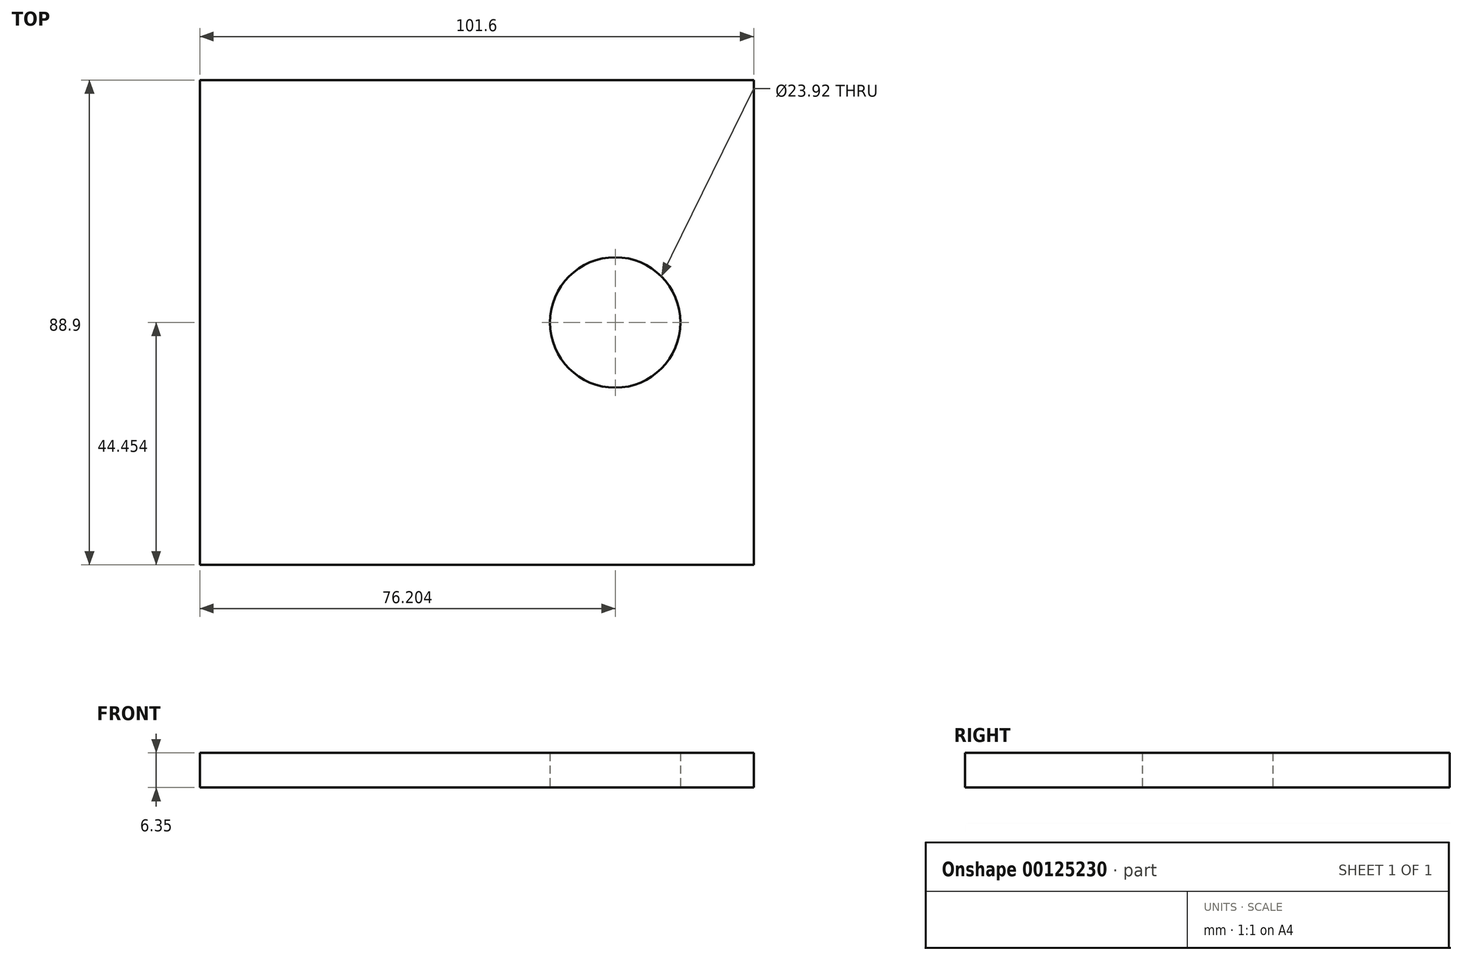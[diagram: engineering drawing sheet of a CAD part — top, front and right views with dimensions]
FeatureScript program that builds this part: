
annotation { "Feature Type Name" : "Feature", "Feature Type Description" : "" }
export const myFeature = defineFeature(function(context is Context, id is Id, definition is map)
    precondition{}
    {
        {
            var Q0;
            Q0=qCreatedBy(makeId("Top.planeOp"),FACE);
            var sketch = newSketch(context, id + "F0", { "sketchPlane" : qUnion([Q0])});
            skLineSegment(sketch, "E0.bottom", {"start": v(-45.86, 38.73) * mm, "end": v(55.74, 38.73) * mm});
            skLineSegment(sketch, "E0.top", {"start": v(-45.86, -50.17) * mm, "end": v(55.74, -50.17) * mm});
            skLineSegment(sketch, "E0.left", {"start": v(-45.86, 38.73) * mm, "end": v(-45.86, -50.17) * mm});
            skLineSegment(sketch, "E0.right", {"start": v(55.74, 38.73) * mm, "end": v(55.74, -50.17) * mm});
            skLineSegment(sketch, "E1", {"start": v(4.94, 38.73) * mm, "end": v(55.74, 38.73) * mm});
            skCircle(sketch, "E2", {"center": v(30.34, -5.72) * mm, "radius": 11.96 * mm});
            skSolve(sketch);
        }
        {
            var Q0;
            {var subQ5=sQuery(id+"F0.wireOp",EDGE,"E0.top");Q0=makeQuery(id+"F0.imprint","IMPRINT",FACE,{"disambiguationData":[TD([[makeQuery(id+"F0.imprint","IMPRINT",EDGE,{"derivedFrom":subQ5}),1.0]])]});}
            var Q1;
            {var subQ0=sQuery(id+"F0.wireOp",EDGE,"E0.bottom");Q1=makeQuery(id+"F0.imprint","IMPRINT",FACE,{"disambiguationData":[TD([[makeQuery(id+"F0.imprint","IMPRINT",EDGE,{"derivedFrom":subQ0}),-1.0]])]});}
            var Q2;
            {var subQ5=sQuery(id+"F0.wireOp",EDGE,"xIj1EgI5-gv82-0Zbr-YIqH-s6Kuo5JfzM8M");Q2=makeQuery(id+"F0.imprint","IMPRINT",FACE,{"disambiguationData":[TD([[makeQuery(id+"F0.imprint","IMPRINT",EDGE,{"derivedFrom":subQ5}),-1.0]])]});}
            var Q3;
            {var subQ1=sQuery(id+"F0.wireOp",EDGE,"E1");var subQ5=sQuery(id+"F0.wireOp",EDGE,"E0.right");var subQ6=makeQuery(id+"F0.imprint","INTERSECT",VERTEX,{"derivedFrom":[subQ5,subQ1]});Q3=makeQuery(id+"F0.imprint","IMPRINT",FACE,{"disambiguationData":[TD([[makeQuery(id+"F0.imprint","IMPRINT",EDGE,{"disambiguationData":[TD([[subQ6,-1.0]])],"derivedFrom":subQ5}),-1.0]])]});}
            extrude(context, id + "F1", {"entities" : qUnion([Q0, Q1, Q2, Q3]), "depth" : 6.35 * mm});
        }
    });
